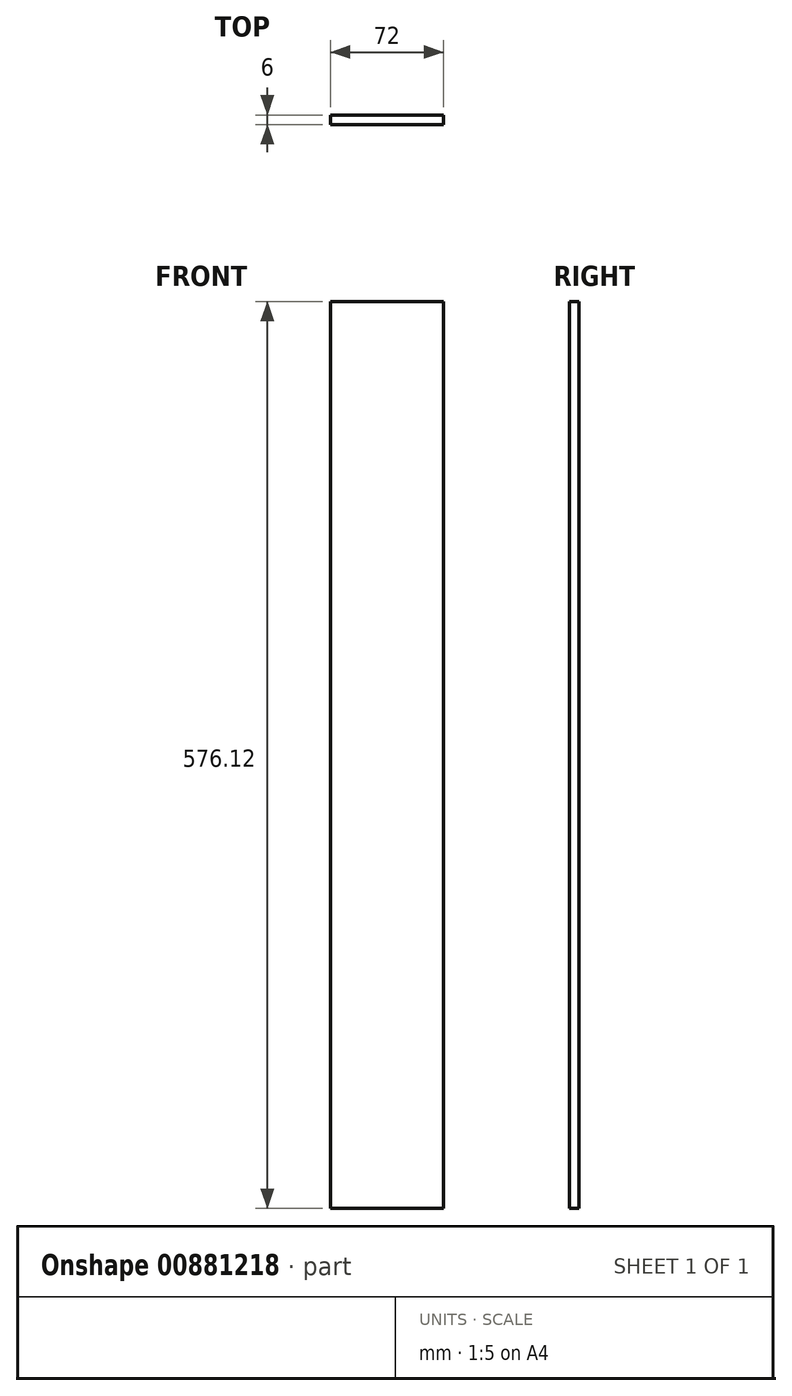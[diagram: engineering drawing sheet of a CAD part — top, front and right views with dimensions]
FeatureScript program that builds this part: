
annotation { "Feature Type Name" : "Feature", "Feature Type Description" : "" }
export const myFeature = defineFeature(function(context is Context, id is Id, definition is map)
    precondition{}
    {
        {
            var Q0;
            Q0=qCreatedBy(makeId("Front.planeOp"),FACE);
            var sketch = newSketch(context, id + "F0", { "sketchPlane" : qUnion([Q0])});
            skLineSegment(sketch, "E0", {"start": v(-36, 288.06) * mm, "end": v(-36, -288.06) * mm});
            skLineSegment(sketch, "E1", {"start": v(36, 288.06) * mm, "end": v(36, -288.06) * mm});
            skLineSegment(sketch, "E2", {"start": v(-36, 288.06) * mm, "end": v(36, 288.06) * mm});
            skLineSegment(sketch, "E3", {"start": v(-36, -288.06) * mm, "end": v(36, -288.06) * mm});
            skSolve(sketch);
        }
        {
            var Q0;
            Q0 = qSketchRegion(id + "F0", true);
            extrude(context, id + "F1", {"entities" : qUnion([Q0]), "depth" : 6 * mm, "offsetDistance" : 25 * mm});
        }
    });
